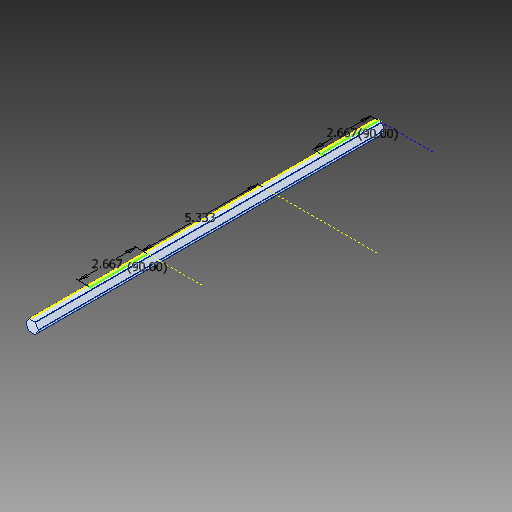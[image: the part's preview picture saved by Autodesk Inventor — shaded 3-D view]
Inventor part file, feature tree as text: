
AUTODESK INVENTOR PART (.ipt)
format: ipt  version: 2017 (Build 210142000, 142)  size: 148,480 bytes
history: native  units: in
note: dims shown in document units (in); Inventor stores cm internally (conversion verified against a paired STEP export)
features: sketch x5, split x1, fillet x1
ambient origin geometry x8: Origin, YZ Plane, XZ Plane, XY Plane, X Axis, Y Axis, Z Axis, Center Point
bodies: Solid1 (feature_tree)
feature tree (7):
  sketch  "Sketch1"  dims[d3=8.5in]
  split  "Split1"
  sketch  "Sketch3"  dims[d7=2.6665in]
  sketch  "Sketch4"  dims[d8=90.0deg]
  sketch  "Sketch5"  dims[d9=2.6665in d10=90.0deg]
  sketch  "Sketch2"  dims[d5=5.333in]
  fillet  "Fillet1"  Radius=16.0in
